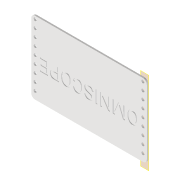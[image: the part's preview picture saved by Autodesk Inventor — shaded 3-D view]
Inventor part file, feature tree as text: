
AUTODESK INVENTOR PART (.ipt)
format: ipt  version: 2022 (Build 260153000, 153)  size: 281,600 bytes
history: native  units: mm
features: extrude x2, sketch x2, reference x2, other x2, plane x1, fillet x1
ambient origin geometry x8: Origin, YZ Plane, XZ Plane, XY Plane, X Axis, Y Axis, Z Axis, Center Point
bodies: Volumenkörper1 (feature_tree)
feature tree (10):
  plane  "Arbeitsebene1"
  extrude  "Extrusion1"  Depth=2.0mm TaperAngle=0.0deg
  fillet  "Rundung1"  Radius=5.0mm
  extrude  "Extrusion2"  [1 undecoded]
  sketch  "Skizze1"  dims[d0=149.0mm d1=2.0mm d2=0.0mm d3=5.0mm]
  reference  "Referenz1"
  reference  "Referenz2"
  sketch  "Skizze2"  dims[d4=1.0mm d5=0.0mm]
  other  "Omnicscope_Xiao.iam"
  other  "Omniscope_USBC_Case:1"
note: 1 required parameter value undecoded (feature->parameter linkage not recoverable at this tier; creation-order binding heuristic only, values carry confidence <= 0.55)
